# Revit family: L-banner 600
name_source: partatom
category: Осветительные приборы
revit_build: Autodesk Revit 2017 (Build: 20160225_1515(x64)
units: mm (PartAtom-declared; Revit-internal decimal feet)

## family parameters
Источник света = Да
Общий = Нет
Основа = Грань
При загрузке вырезать с полостями = Нет
Размер круглого соединителя = Использовать диаметр
Тип детали = Нормальный
Точка расчета площади = Нет

## types (8) — shared parameters
L = 68 мм
Видимая форма излучения при визуализации = Нет
Изготовитель = LEDEL
Излучение по диаметру окружности = 298 мм
Комментарии к типоразмеру = Прожекторы
Отметка по умолчанию = 1219 мм
Полная установленная мощность = 600 В·А
Светофильтр = 16777215
Смещение цветовой температуры при затухании лампы = <Нет>
Угол наклона = 90.00°

## per-type parameters (varying)
| type | Артикул | Файл фотометрической сетки |
| L-banner 600-K15-5.0K | 409004 | L-banner 600-600-K15-5.0K-04.ies |
| L-banner 600-K15-4.0K | 621160002744200 | L-banner 600-600-K15-4.0K-04.ies |
| L-banner 600-Г30-4.0K | 621160004744200 | L-banner 600-600-G30-4.0K-04.ies |
| L-banner 600-Г30-5.0K | 409003 | L-banner 600-600-G30-5.0K-04.ies |
| L-banner 600-Г60-4.0K | 621160006744200 | L-banner 600-600-G60-4.0K-04.ies |
| L-banner 600-Г60-5.0K | 409002 | L-banner 600-600-G60-5.0K-04.ies |
| L-banner 600-К8-4.0K |  | L-banner 600-600-K8-4.0K-04.ies |
| L-banner 600-К8-5.0K | 409001 | L-banner 600-600-K8-5.0K-04.ies |

## geometry (parser evidence)
native form markers: Sweep x3
no freeform markers — native parametric forms only
